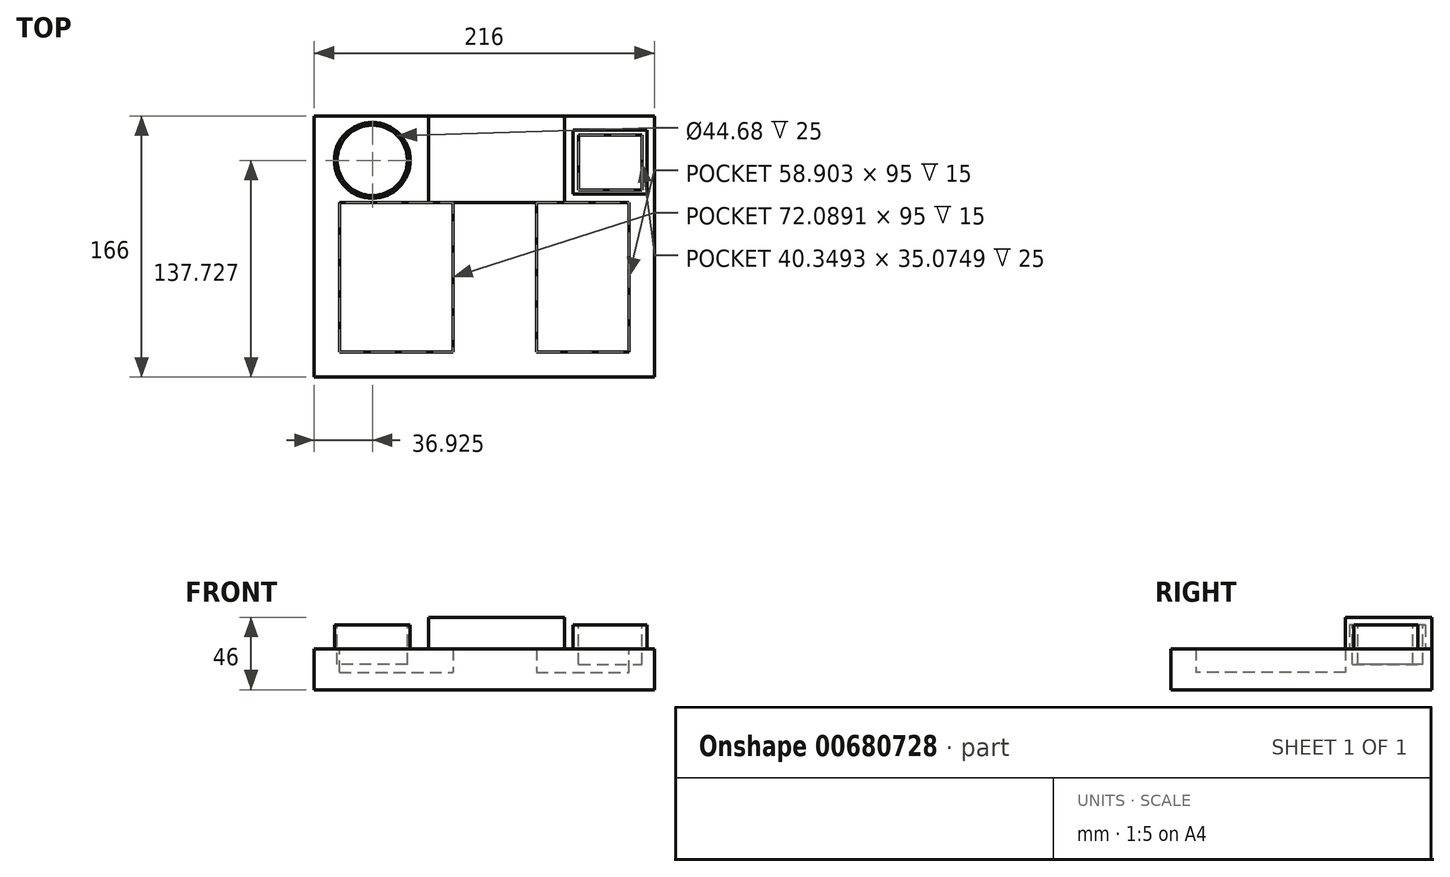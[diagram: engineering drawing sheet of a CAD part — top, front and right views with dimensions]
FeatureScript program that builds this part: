
annotation { "Feature Type Name" : "Feature", "Feature Type Description" : "" }
export const myFeature = defineFeature(function(context is Context, id is Id, definition is map)
    precondition{}
    {
        {
            var Q0;
            Q0=qCreatedBy(makeId("Top.planeOp"),FACE);
            var sketch = newSketch(context, id + "F0", { "sketchPlane" : qUnion([Q0])});
            skLineSegment(sketch, "E0.bottom", {"start": v(-143.6, 127.7) * mm, "end": v(72.4, 127.7) * mm});
            skLineSegment(sketch, "E0.top", {"start": v(-143.6, -38.3) * mm, "end": v(72.4, -38.3) * mm});
            skLineSegment(sketch, "E0.left", {"start": v(-143.6, 127.7) * mm, "end": v(-143.6, -38.3) * mm});
            skLineSegment(sketch, "E0.right", {"start": v(72.4, 127.7) * mm, "end": v(72.4, -38.3) * mm});
            skSolve(sketch);
        }
        {
            var Q0;
            Q0 = qSketchRegion(id + "F0", true);
            extrude(context, id + "F1", {"entities" : qUnion([Q0]), "depth" : 26 * mm, "offsetDistance" : 25 * mm});
        }
        {
            var Q0;
            Q0=makeQuery(id+"F1.opExtrude","CAP_FACE",FACE,{"disambiguationData":[OSD([sQuery(id+"F0.wireOp",EDGE,"E0.bottom"),sQuery(id+"F0.wireOp",EDGE,"E0.top"),sQuery(id+"F0.wireOp",EDGE,"E0.left"),sQuery(id+"F0.wireOp",EDGE,"E0.right")])],"isStart":false});
            var sketch = newSketch(context, id + "F2", { "sketchPlane" : qUnion([Q0])});
            skLineSegment(sketch, "E1.bottom", {"start": v(-127.6, 72.7) * mm, "end": v(56.4, 72.7) * mm});
            skLineSegment(sketch, "E1.top", {"start": v(-127.6, -22.3) * mm, "end": v(56.4, -22.3) * mm});
            skLineSegment(sketch, "E1.left", {"start": v(-127.6, 72.7) * mm, "end": v(-127.6, -22.3) * mm});
            skLineSegment(sketch, "E1.right", {"start": v(56.4, 72.7) * mm, "end": v(56.4, -22.3) * mm});
            skSolve(sketch);
        }
        {
            var Q0;
            Q0 = qSketchRegion(id + "F2", true);
            extrude(context, id + "F3", {"entities" : qUnion([Q0]), "operationType" : NewBodyOperationType.REMOVE, "oppositeDirection" : true, "depth" : 15 * mm, "offsetDistance" : 25 * mm});
        }
        {
            var Q0;
            Q0=makeQuery(id+"F1.opExtrude","CAP_FACE",FACE,{"disambiguationData":[OSD([sQuery(id+"F0.wireOp",EDGE,"E0.bottom"),sQuery(id+"F0.wireOp",EDGE,"E0.top"),sQuery(id+"F0.wireOp",EDGE,"E0.left"),sQuery(id+"F0.wireOp",EDGE,"E0.right")])],"isStart":false});
            var sketch = newSketch(context, id + "F4", { "sketchPlane" : qUnion([Q0])});
            skLineSegment(sketch, "E2.bottom", {"start": v(-70.84, 127.7) * mm, "end": v(15.34, 127.7) * mm});
            skLineSegment(sketch, "E2.top", {"start": v(-70.84, 72.7) * mm, "end": v(15.34, 72.7) * mm});
            skLineSegment(sketch, "E2.left", {"start": v(-70.84, 127.7) * mm, "end": v(-70.84, 72.7) * mm});
            skLineSegment(sketch, "E2.right", {"start": v(15.34, 127.7) * mm, "end": v(15.34, 72.7) * mm});
            skSolve(sketch);
        }
        {
            var Q0;
            Q0 = qSketchRegion(id + "F4", true);
            extrude(context, id + "F5", {"entities" : qUnion([Q0]), "operationType" : NewBodyOperationType.ADD, "depth" : 20 * mm, "offsetDistance" : 25 * mm});
        }
        {
            var Q0;
            Q0=makeQuery(id+"F3.boolean.opBoolean","COPY",FACE,{"derivedFrom":makeQuery(id+"F3.opExtrude","CAP_FACE",FACE,{"disambiguationData":[OSD([sQuery(id+"F2.wireOp",EDGE,"E1.bottom"),sQuery(id+"F2.wireOp",EDGE,"E1.top"),sQuery(id+"F2.wireOp",EDGE,"E1.left"),sQuery(id+"F2.wireOp",EDGE,"E1.right")])],"isStart":false})});
            var sketch = newSketch(context, id + "F6", { "sketchPlane" : qUnion([Q0])});
            skLineSegment(sketch, "E3.bottom", {"start": v(-55.5, 72.7) * mm, "end": v(-2.5, 72.7) * mm});
            skLineSegment(sketch, "E3.top", {"start": v(-55.5, -22.3) * mm, "end": v(-2.5, -22.3) * mm});
            skLineSegment(sketch, "E3.left", {"start": v(-55.5, 72.7) * mm, "end": v(-55.5, -22.3) * mm});
            skLineSegment(sketch, "E3.right", {"start": v(-2.5, 72.7) * mm, "end": v(-2.5, -22.3) * mm});
            skSolve(sketch);
        }
        {
            var Q0;
            Q0 = qSketchRegion(id + "F6", true);
            extrude(context, id + "F7", {"entities" : qUnion([Q0]), "operationType" : NewBodyOperationType.ADD, "depth" : 15 * mm, "offsetDistance" : 25 * mm});
        }
        {
            var Q0;
            Q0=makeQuery(id+"F7.boolean.opBoolean","MERGE",FACE,{"derivedFrom":[makeQuery(id+"F1.opExtrude","CAP_FACE",FACE,{"disambiguationData":[OSD([sQuery(id+"F0.wireOp",EDGE,"E0.bottom"),sQuery(id+"F0.wireOp",EDGE,"E0.top"),sQuery(id+"F0.wireOp",EDGE,"E0.left"),sQuery(id+"F0.wireOp",EDGE,"E0.right")])],"isStart":false}),makeQuery(id+"F7.opExtrude","CAP_FACE",FACE,{"disambiguationData":[OSD([sQuery(id+"F6.wireOp",EDGE,"E3.bottom"),sQuery(id+"F6.wireOp",EDGE,"E3.top"),sQuery(id+"F6.wireOp",EDGE,"E3.left"),sQuery(id+"F6.wireOp",EDGE,"E3.right")])],"isStart":false})]});
            var sketch = newSketch(context, id + "F8", { "sketchPlane" : qUnion([Q0])});
            skCircle(sketch, "E4", {"center": v(-106.67, 99.43) * mm, "radius": 24.13 * mm});
            skSolve(sketch);
        }
        {
            var Q0;
            Q0 = qSketchRegion(id + "F8", true);
            extrude(context, id + "F9", {"entities" : qUnion([Q0]), "operationType" : NewBodyOperationType.ADD, "depth" : 15 * mm, "offsetDistance" : 25 * mm});
        }
        {
            var Q0;
            Q0=makeQuery(id+"F9.opExtrude","CAP_FACE",FACE,{"disambiguationData":[OSD([sQuery(id+"F8.wireOp",EDGE,"E4")])],"isStart":false});
            var sketch = newSketch(context, id + "F10", { "sketchPlane" : qUnion([Q0])});
            skCircle(sketch, "E5", {"center": v(-106.67, 99.43) * mm, "radius": 22.34 * mm});
            skSolve(sketch);
        }
        {
            var Q0;
            Q0 = qSketchRegion(id + "F10", true);
            extrude(context, id + "F11", {"entities" : qUnion([Q0]), "operationType" : NewBodyOperationType.REMOVE, "oppositeDirection" : true, "depth" : 25 * mm, "offsetDistance" : 25 * mm});
        }
        {
            var Q0;
            Q0=makeQuery(id+"F7.boolean.opBoolean","MERGE",FACE,{"derivedFrom":[makeQuery(id+"F1.opExtrude","CAP_FACE",FACE,{"disambiguationData":[OSD([sQuery(id+"F0.wireOp",EDGE,"E0.bottom"),sQuery(id+"F0.wireOp",EDGE,"E0.top"),sQuery(id+"F0.wireOp",EDGE,"E0.left"),sQuery(id+"F0.wireOp",EDGE,"E0.right")])],"isStart":false}),makeQuery(id+"F7.opExtrude","CAP_FACE",FACE,{"disambiguationData":[OSD([sQuery(id+"F6.wireOp",EDGE,"E3.bottom"),sQuery(id+"F6.wireOp",EDGE,"E3.top"),sQuery(id+"F6.wireOp",EDGE,"E3.left"),sQuery(id+"F6.wireOp",EDGE,"E3.right")])],"isStart":false})]});
            var sketch = newSketch(context, id + "F12", { "sketchPlane" : qUnion([Q0])});
            skLineSegment(sketch, "E6.bottom", {"start": v(20.97, 118.65) * mm, "end": v(67.77, 118.65) * mm});
            skLineSegment(sketch, "E6.top", {"start": v(20.97, 78.07) * mm, "end": v(67.77, 78.07) * mm});
            skLineSegment(sketch, "E6.left", {"start": v(20.97, 118.65) * mm, "end": v(20.97, 78.07) * mm});
            skLineSegment(sketch, "E6.right", {"start": v(67.77, 118.65) * mm, "end": v(67.77, 78.07) * mm});
            skSolve(sketch);
        }
        {
            var Q0;
            Q0 = qSketchRegion(id + "F12", true);
            extrude(context, id + "F13", {"entities" : qUnion([Q0]), "operationType" : NewBodyOperationType.ADD, "depth" : 15 * mm, "offsetDistance" : 25 * mm});
        }
        {
            var Q0;
            Q0=makeQuery(id+"F13.opExtrude","CAP_FACE",FACE,{"disambiguationData":[OSD([sQuery(id+"F12.wireOp",EDGE,"E6.bottom"),sQuery(id+"F12.wireOp",EDGE,"E6.top"),sQuery(id+"F12.wireOp",EDGE,"E6.left"),sQuery(id+"F12.wireOp",EDGE,"E6.right")])],"isStart":false});
            var sketch = newSketch(context, id + "F14", { "sketchPlane" : qUnion([Q0])});
            skLineSegment(sketch, "E7.bottom", {"start": v(24.4, 115.51) * mm, "end": v(64.75, 115.51) * mm});
            skLineSegment(sketch, "E7.top", {"start": v(24.4, 80.44) * mm, "end": v(64.75, 80.44) * mm});
            skLineSegment(sketch, "E7.left", {"start": v(24.4, 115.51) * mm, "end": v(24.4, 80.44) * mm});
            skLineSegment(sketch, "E7.right", {"start": v(64.75, 115.51) * mm, "end": v(64.75, 80.44) * mm});
            skSolve(sketch);
        }
        {
            var Q0;
            Q0 = qSketchRegion(id + "F14", true);
            extrude(context, id + "F15", {"entities" : qUnion([Q0]), "operationType" : NewBodyOperationType.REMOVE, "oppositeDirection" : true, "depth" : 25 * mm, "offsetDistance" : 25 * mm});
        }
    });
